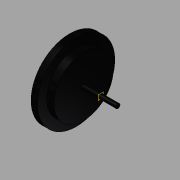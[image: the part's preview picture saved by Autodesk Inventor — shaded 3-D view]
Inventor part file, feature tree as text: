
AUTODESK INVENTOR PART (.ipt)
format: ipt  version: 2015 (Build 190159000, 159)  size: 140,288 bytes
history: native  units: in
note: dims shown in document units (in); Inventor stores cm internally (conversion verified against a paired STEP export)
features: sketch x5, other x3, plane x1
ambient origin geometry x8: Origin, YZ Plane, XZ Plane, XY Plane, X Axis, Y Axis, Z Axis, Center Point
bodies: Solid1 (feature_tree)
feature tree (9):
  other  "rueda.ipt"
  other  "Solid1::rueda.ipt"
  other  "TaggingFeature1"
  sketch  "Sketch2"  dims[d0=0.3937in]
  sketch  "Sketch3"
  sketch  "Sketch7"
  sketch  "Sketch12"
  sketch  "Sketch13"
  plane  "Work Plane1"
